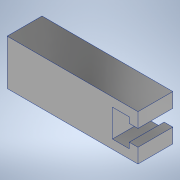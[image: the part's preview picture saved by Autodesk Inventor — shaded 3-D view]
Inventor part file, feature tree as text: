
AUTODESK INVENTOR PART (.ipt)
format: ipt  version: 2022 (Build 260153000, 153)  size: 132,608 bytes
history: native  units: mm
features: extrude x2, sketch x2
ambient origin geometry x8: Origin, YZ Plane, XZ Plane, XY Plane, X Axis, Y Axis, Z Axis, Center Point
bodies: Body1 (feature_tree)
feature tree (4):
  extrude  "Extrusion2"  Depth=5.8mm
  extrude  "Extrusion4"  Depth=12.0mm TaperAngle=0.0deg
  sketch  "Sketch5"  dims[d41=5.8mm d48=44.0mm]
  sketch  "Sketch7"  dims[d50=3.0mm d56=12.0mm d57=0.0mm d63=45.0mm d67=15.6mm d71=0.0mm d72=36.2mm d78=0.0mm d79=0.0mm d80=5.6mm d81=9.5mm]
